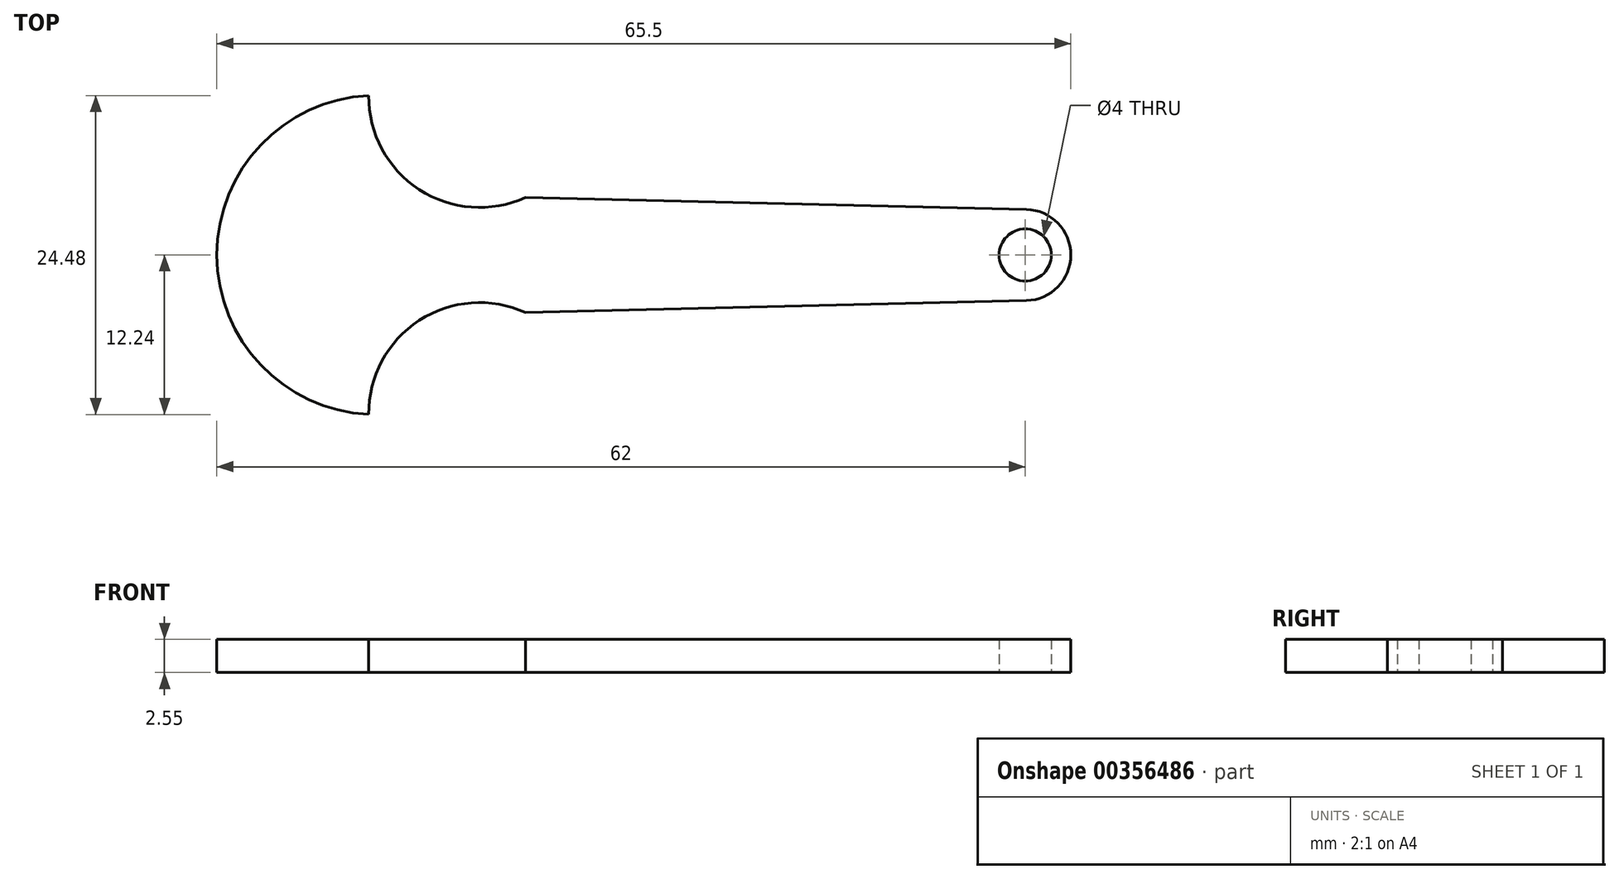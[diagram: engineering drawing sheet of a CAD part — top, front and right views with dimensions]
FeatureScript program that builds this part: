
annotation { "Feature Type Name" : "Feature", "Feature Type Description" : "" }
export const myFeature = defineFeature(function(context is Context, id is Id, definition is map)
    precondition{}
    {
        {
            var Q0;
            Q0=qCreatedBy(makeId("Top.planeOp"),FACE);
            var sketch = newSketch(context, id + "F0", { "sketchPlane" : qUnion([Q0])});
            skArc(sketch, "E0", {"start": v(-0.6, 12.24) * mm, "mid": v(-12.25, 0) * mm, "end": v(-0.6, -12.24) * mm});
            skLineSegment(sketch, "E1", {"start": v(-24.87, 0) * mm, "end": v(156.4, 0) * mm, "construction": true});
            skArc(sketch, "E2", {"start": v(49.83, -3.5) * mm, "mid": v(53.25, 0) * mm, "end": v(49.83, 3.5) * mm});
            skCircle(sketch, "E3", {"center": v(49.75, 0) * mm, "radius": 2 * mm});
            skLineSegment(sketch, "E4", {"start": v(7.9, 24.11) * mm, "end": v(7.9, -18.76) * mm, "construction": true});
            skArc(sketch, "E5", {"start": v(-0.6, 12.24) * mm, "mid": v(3.27, 5.02) * mm, "end": v(11.43, 4.42) * mm});
            skArc(sketch, "E6.MirrorC", {"start": v(-0.6, -12.24) * mm, "mid": v(3.27, -5.02) * mm, "end": v(11.43, -4.42) * mm});
            skLineSegment(sketch, "E7", {"start": v(11.43, 4.42) * mm, "end": v(49.83, 3.5) * mm});
            skLineSegment(sketch, "E8", {"start": v(11.43, -4.42) * mm, "end": v(49.83, -3.5) * mm});
            skSolve(sketch);
        }
        {
            var Q0;
            Q0=makeQuery(id+"F0.imprint","IMPRINT",FACE,{"disambiguationData":[TD([[makeQuery(id+"F0.imprint","IMPRINT",EDGE,{"derivedFrom":sQuery(id+"F0.wireOp",EDGE,"E0")}),1.0]])]});
            extrude(context, id + "F1", {"entities" : qUnion([Q0]), "depth" : 2.55 * mm});
        }
    });
